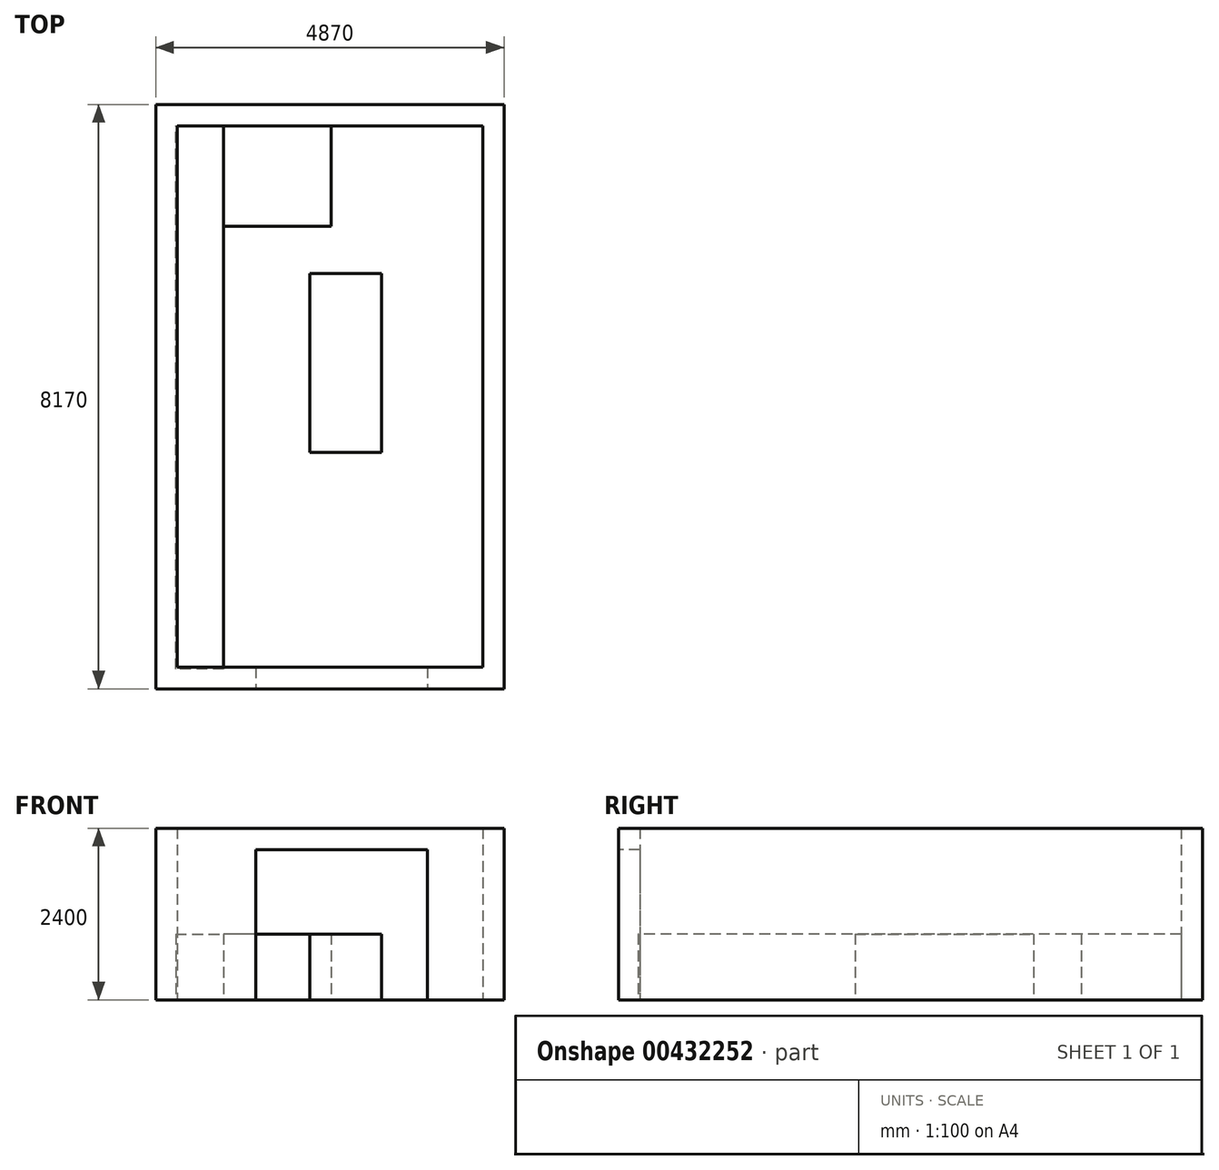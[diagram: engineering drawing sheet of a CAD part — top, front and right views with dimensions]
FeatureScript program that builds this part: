
annotation { "Feature Type Name" : "Feature", "Feature Type Description" : "" }
export const myFeature = defineFeature(function(context is Context, id is Id, definition is map)
    precondition{}
    {
        {
            var Q0;
            Q0=qCreatedBy(makeId("Top.planeOp"),FACE);
            var sketch = newSketch(context, id + "F0", { "sketchPlane" : qUnion([Q0])});
            skLineSegment(sketch, "E0.bottom", {"start": v(0, 0) * mm, "end": v(4870, 0) * mm});
            skLineSegment(sketch, "E0.top", {"start": v(0, 8170) * mm, "end": v(4870, 8170) * mm});
            skLineSegment(sketch, "E0.left", {"start": v(0, 0) * mm, "end": v(0, 8170) * mm});
            skLineSegment(sketch, "E0.right", {"start": v(4870, 0) * mm, "end": v(4870, 8170) * mm});
            skLineSegment(sketch, "E1.bottom", {"start": v(300, 7870) * mm, "end": v(4570, 7870) * mm});
            skLineSegment(sketch, "E1.top", {"start": v(300, 300) * mm, "end": v(4570, 300) * mm});
            skLineSegment(sketch, "E1.left", {"start": v(300, 7870) * mm, "end": v(300, 300) * mm});
            skLineSegment(sketch, "E1.right", {"start": v(4570, 7870) * mm, "end": v(4570, 300) * mm});
            skLineSegment(sketch, "E2", {"start": v(300, 7870) * mm, "end": v(950, 7870) * mm});
            skSolve(sketch);
        }
        {
            var Q0;
            Q0=makeQuery(id+"F0.imprint","IMPRINT",FACE,{"disambiguationData":[TD([[makeQuery(id+"F0.imprint","IMPRINT",EDGE,{"derivedFrom":sQuery(id+"F0.wireOp",EDGE,"E0.bottom")}),1.0]])]});
            extrude(context, id + "F1", {"entities" : qUnion([Q0]), "depth" : 2400 * mm});
        }
        {
            var Q0;
            Q0=qCreatedBy(makeId("Top.planeOp"),FACE);
            var sketch = newSketch(context, id + "F2", { "sketchPlane" : qUnion([Q0])});
            skLineSegment(sketch, "E3", {"start": v(950, 7870) * mm, "end": v(950, 651.99) * mm});
            skLineSegment(sketch, "E4", {"start": v(950, 651.99) * mm, "end": v(950, 275.54) * mm});
            skLineSegment(sketch, "E5", {"start": v(950, 275.54) * mm, "end": v(278.45, 275.54) * mm});
            skLineSegment(sketch, "E6", {"start": v(278.45, 275.54) * mm, "end": v(278.45, 7870) * mm});
            skLineSegment(sketch, "E7", {"start": v(278.45, 7870) * mm, "end": v(950, 7870) * mm});
            skSolve(sketch);
        }
        {
            var Q0;
            Q0 = qSketchRegion(id + "F2", true);
            extrude(context, id + "F3", {"entities" : qUnion([Q0]), "depth" : 920 * mm});
        }
        {
            var Q0;
            Q0=makeQuery(id+"F1.opExtrude","SWEPT_FACE",FACE,{"disambiguationData":[OSD([sQuery(id+"F0.wireOp",EDGE,"E0.bottom")])]});
            var sketch = newSketch(context, id + "F4", { "sketchPlane" : qUnion([Q0])});
            skLineSegment(sketch, "E8.bottom", {"start": v(1395.34, 0) * mm, "end": v(3795.34, 0) * mm});
            skLineSegment(sketch, "E8.top", {"start": v(1395.34, 2100) * mm, "end": v(3795.34, 2100) * mm});
            skLineSegment(sketch, "E8.left", {"start": v(1395.34, 0) * mm, "end": v(1395.34, 2100) * mm});
            skLineSegment(sketch, "E8.right", {"start": v(3795.34, 0) * mm, "end": v(3795.34, 2100) * mm});
            skSolve(sketch);
        }
        {
            var Q0;
            Q0 = qSketchRegion(id + "F4", true);
            extrude(context, id + "F5", {"entities" : qUnion([Q0]), "operationType" : NewBodyOperationType.REMOVE, "oppositeDirection" : true, "depth" : 510 * mm});
        }
        {
            var Q0;
            Q0=qCreatedBy(makeId("Top.planeOp"),FACE);
            var sketch = newSketch(context, id + "F6", { "sketchPlane" : qUnion([Q0])});
            skLineSegment(sketch, "E9", {"start": v(2156.29, 507.33) * mm, "end": v(2156.29, 3307.33) * mm, "construction": true});
            skLineSegment(sketch, "E10", {"start": v(2156.29, 3307.33) * mm, "end": v(956.29, 3307.33) * mm, "construction": true});
            skLineSegment(sketch, "E11.bottom", {"start": v(2156.29, 3307.33) * mm, "end": v(3156.29, 3307.33) * mm});
            skLineSegment(sketch, "E11.top", {"start": v(2156.29, 5807.33) * mm, "end": v(3156.29, 5807.33) * mm});
            skLineSegment(sketch, "E11.left", {"start": v(2156.29, 3307.33) * mm, "end": v(2156.29, 5807.33) * mm});
            skLineSegment(sketch, "E11.right", {"start": v(3156.29, 3307.33) * mm, "end": v(3156.29, 5807.33) * mm});
            skSolve(sketch);
        }
        {
            var Q0;
            Q0 = qSketchRegion(id + "F6", true);
            extrude(context, id + "F7", {"entities" : qUnion([Q0]), "operationType" : NewBodyOperationType.ADD, "depth" : 920 * mm});
        }
        {
            var Q0;
            Q0=makeQuery(id+"F3.opExtrude","SWEPT_FACE",FACE,{"disambiguationData":[OSD([sQuery(id+"F2.wireOp",EDGE,"E3"),sQuery(id+"F2.wireOp",EDGE,"E4")])]});
            var sketch = newSketch(context, id + "F8", { "sketchPlane" : qUnion([Q0])});
            skLineSegment(sketch, "E12.bottom", {"start": v(7870, 920) * mm, "end": v(6470, 920) * mm});
            skLineSegment(sketch, "E12.top", {"start": v(7870, 0) * mm, "end": v(6470, 0) * mm});
            skLineSegment(sketch, "E12.left", {"start": v(7870, 920) * mm, "end": v(7870, 0) * mm});
            skLineSegment(sketch, "E12.right", {"start": v(6470, 920) * mm, "end": v(6470, 0) * mm});
            skSolve(sketch);
        }
        {
            var Q0;
            Q0 = qSketchRegion(id + "F8", true);
            extrude(context, id + "F9", {"entities" : qUnion([Q0]), "depth" : 1500 * mm});
        }
    });
